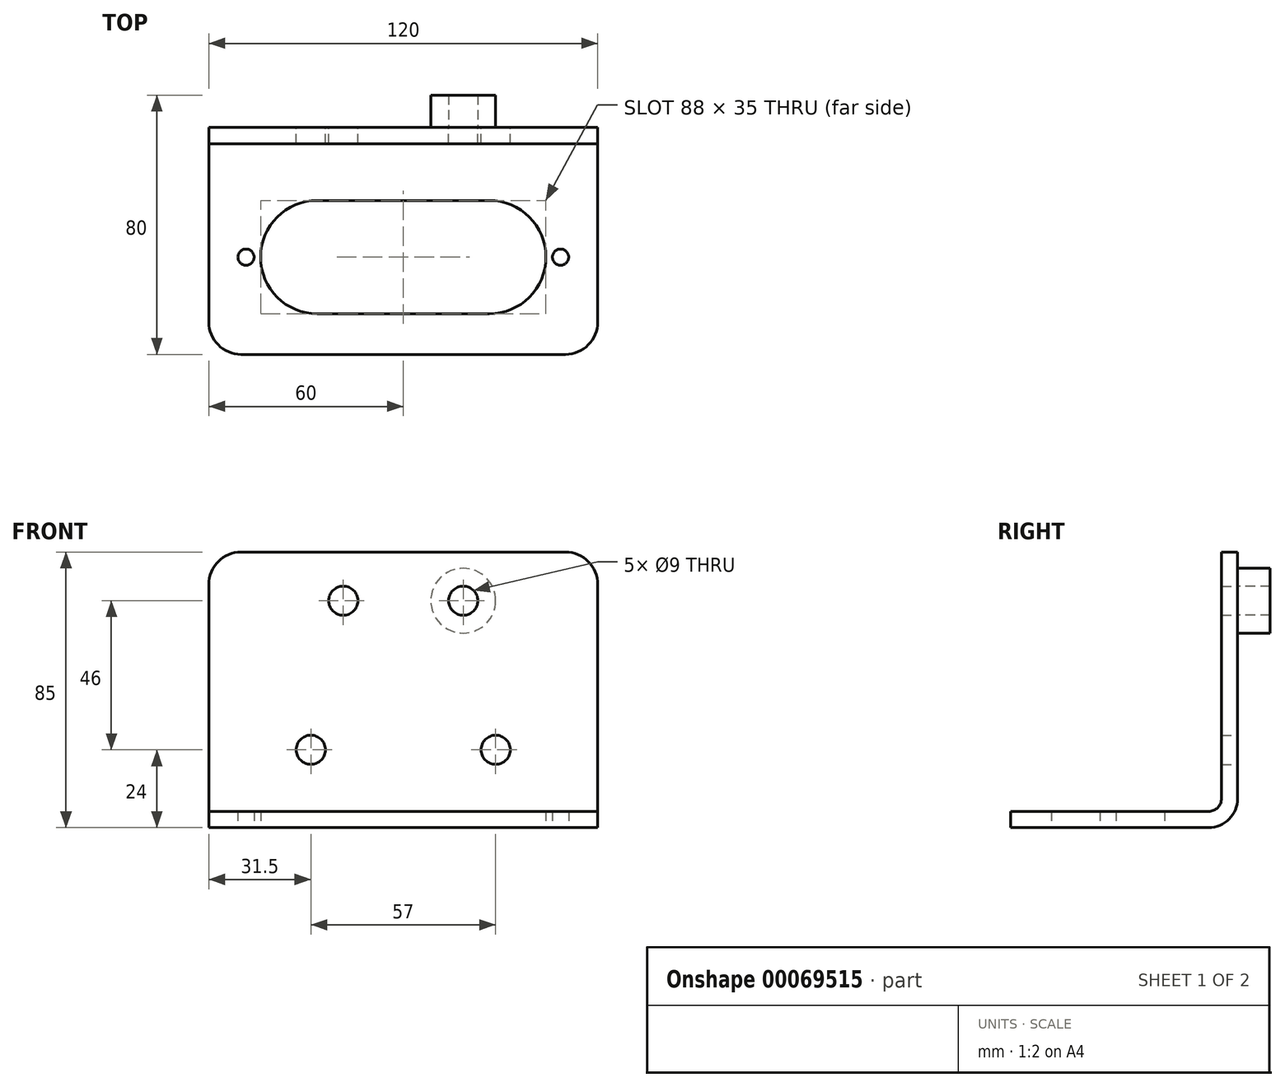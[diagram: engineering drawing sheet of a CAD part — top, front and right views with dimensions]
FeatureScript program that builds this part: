
annotation { "Feature Type Name" : "Feature", "Feature Type Description" : "" }
export const myFeature = defineFeature(function(context is Context, id is Id, definition is map)
    precondition{}
    {
        {
            var Q0;
            Q0=qCreatedBy(makeId("Top.planeOp"),FACE);
            var sketch = newSketch(context, id + "F0", { "sketchPlane" : qUnion([Q0])});
            skLineSegment(sketch, "E0", {"start": v(-60, 0) * mm, "end": v(-60, -60) * mm});
            skArc(sketch, "E1", {"start": v(-60, -60) * mm, "mid": v(-57.07, -67.07) * mm, "end": v(-50, -70) * mm});
            skLineSegment(sketch, "E2", {"start": v(-50, -70) * mm, "end": v(50, -70) * mm});
            skArc(sketch, "E3", {"start": v(50, -70) * mm, "mid": v(57.07, -67.07) * mm, "end": v(60, -60) * mm});
            skLineSegment(sketch, "E4", {"start": v(60, -60) * mm, "end": v(60, 0) * mm});
            skLineSegment(sketch, "E5", {"start": v(60, 0) * mm, "end": v(60, 75) * mm});
            skArc(sketch, "E6", {"start": v(60, 75) * mm, "mid": v(57.07, 82.07) * mm, "end": v(50, 85) * mm});
            skLineSegment(sketch, "E7", {"start": v(50, 85) * mm, "end": v(-50, 85) * mm});
            skArc(sketch, "E8", {"start": v(-50, 85) * mm, "mid": v(-57.07, 82.07) * mm, "end": v(-60, 75) * mm});
            skLineSegment(sketch, "E9", {"start": v(-60, 75) * mm, "end": v(-60, 0) * mm});
            skLineSegment(sketch, "E10", {"start": v(26.5, -22.5) * mm, "end": v(-26.5, -22.5) * mm});
            skArc(sketch, "E11", {"start": v(-26.5, -22.5) * mm, "mid": v(-44, -40) * mm, "end": v(-26.5, -57.5) * mm});
            skLineSegment(sketch, "E12", {"start": v(-26.5, -57.5) * mm, "end": v(26.5, -57.5) * mm});
            skArc(sketch, "E13", {"start": v(26.5, -57.5) * mm, "mid": v(44, -40) * mm, "end": v(26.5, -22.5) * mm});
            skCircle(sketch, "E14", {"center": v(-48.5, -40) * mm, "radius": 2.5 * mm});
            skCircle(sketch, "E15", {"center": v(48.5, -40) * mm, "radius": 2.5 * mm});
            skCircle(sketch, "E16", {"center": v(18.5, 70) * mm, "radius": 4.5 * mm});
            skCircle(sketch, "E17", {"center": v(28.5, 24) * mm, "radius": 4.5 * mm});
            skLineSegment(sketch, "E18", {"start": v(-60, 0) * mm, "end": v(60, 0) * mm});
            skLineSegment(sketch, "E19", {"start": v(-48.5, -40) * mm, "end": v(48.5, -40) * mm, "construction": true});
            skLineSegment(sketch, "E20", {"start": v(0, 85) * mm, "end": v(0, -70) * mm, "construction": true});
            skCircle(sketch, "E21.MirrorC", {"center": v(-18.5, 70) * mm, "radius": 4.5 * mm});
            skCircle(sketch, "E22.MirrorC", {"center": v(-28.5, 24) * mm, "radius": 4.5 * mm});
            skSolve(sketch);
        }
        {
            var Q0;
            Q0=makeQuery(id+"F0.imprint","IMPRINT",FACE,{"disambiguationData":[TD([[makeQuery(id+"F0.imprint","IMPRINT",EDGE,{"derivedFrom":sQuery(id+"F0.wireOp",EDGE,"E0")}),1.0]])]});
            extrude(context, id + "F1", {"entities" : qUnion([Q0]), "depth" : 5 * mm});
        }
        {
            var Q0;
            Q0=makeQuery(id+"F0.imprint","IMPRINT",FACE,{"disambiguationData":[TD([[makeQuery(id+"F0.imprint","IMPRINT",EDGE,{"derivedFrom":sQuery(id+"F0.wireOp",EDGE,"E5")}),1.0]])]});
            extrude(context, id + "F2", {"entities" : qUnion([Q0]), "depth" : 5 * mm});
        }
        {
            var Q0;
            Q0=makeQuery(id+"F2.opExtrude","SWEPT_BODY",BODY,{"disambiguationData":[OSD([sQuery(id+"F0.wireOp",EDGE,"dcd2564a-1519-4e3c-a726-8554a83bfc4d"),sQuery(id+"F0.wireOp",EDGE,"E5"),sQuery(id+"F0.wireOp",EDGE,"E6"),sQuery(id+"F0.wireOp",EDGE,"E7"),sQuery(id+"F0.wireOp",EDGE,"E8"),sQuery(id+"F0.wireOp",EDGE,"E9"),sQuery(id+"F0.wireOp",EDGE,"f265843f-5eec-4993-bfec-df9498e86563"),sQuery(id+"F0.wireOp",EDGE,"E16"),sQuery(id+"F0.wireOp",EDGE,"E17"),sQuery(id+"F0.wireOp",EDGE,"E18")])]});
            var Q1;
            Q1=makeQuery(id+"F1.opExtrude","CAP_EDGE",EDGE,{"disambiguationData":[OSD([sQuery(id+"F0.wireOp",EDGE,"E18")])],"isStart":false});
            transform(context, id + "F3", {"entities" : qUnion([Q0]), "transformType" : TransformType.ROTATION, "transformAxis" : qUnion([Q1]), "angle" : 90 * degree, "makeCopy" : false});
        }
        {
            var Q0;
            Q0=makeQuery(id+"F2.opExtrude","SWEPT_BODY",BODY,{"disambiguationData":[OSD([sQuery(id+"F0.wireOp",EDGE,"dcd2564a-1519-4e3c-a726-8554a83bfc4d"),sQuery(id+"F0.wireOp",EDGE,"E5"),sQuery(id+"F0.wireOp",EDGE,"E6"),sQuery(id+"F0.wireOp",EDGE,"E7"),sQuery(id+"F0.wireOp",EDGE,"E8"),sQuery(id+"F0.wireOp",EDGE,"E9"),sQuery(id+"F0.wireOp",EDGE,"f265843f-5eec-4993-bfec-df9498e86563"),sQuery(id+"F0.wireOp",EDGE,"E16"),sQuery(id+"F0.wireOp",EDGE,"E17"),sQuery(id+"F0.wireOp",EDGE,"E18")])]});
            transform(context, id + "F4", {"entities" : qUnion([Q0]), "transformType" : TransformType.TRANSLATION_3D, "dx" : 0 * mm, "dy" : -5 * mm, "dz" : -5 * mm, "makeCopy" : false});
        }
        {
            var Q0;
            Q0=makeQuery(id+"F1.opExtrude","SWEPT_BODY",BODY,{"disambiguationData":[OSD([sQuery(id+"F0.wireOp",EDGE,"E0"),sQuery(id+"F0.wireOp",EDGE,"E1"),sQuery(id+"F0.wireOp",EDGE,"E2"),sQuery(id+"F0.wireOp",EDGE,"E3"),sQuery(id+"F0.wireOp",EDGE,"E4"),sQuery(id+"F0.wireOp",EDGE,"b944222a-91ae-40db-8da9-c3a74cff1a19"),sQuery(id+"F0.wireOp",EDGE,"52282161-0c92-4602-815b-eede0631a33d"),sQuery(id+"F0.wireOp",EDGE,"E10"),sQuery(id+"F0.wireOp",EDGE,"E11"),sQuery(id+"F0.wireOp",EDGE,"E12"),sQuery(id+"F0.wireOp",EDGE,"E13"),sQuery(id+"F0.wireOp",EDGE,"E14"),sQuery(id+"F0.wireOp",EDGE,"E15"),sQuery(id+"F0.wireOp",EDGE,"E18")])]});
            var Q1;
            Q1=makeQuery(id+"F2.opExtrude","SWEPT_BODY",BODY,{"disambiguationData":[OSD([sQuery(id+"F0.wireOp",EDGE,"dcd2564a-1519-4e3c-a726-8554a83bfc4d"),sQuery(id+"F0.wireOp",EDGE,"E5"),sQuery(id+"F0.wireOp",EDGE,"E6"),sQuery(id+"F0.wireOp",EDGE,"E7"),sQuery(id+"F0.wireOp",EDGE,"E8"),sQuery(id+"F0.wireOp",EDGE,"E9"),sQuery(id+"F0.wireOp",EDGE,"f265843f-5eec-4993-bfec-df9498e86563"),sQuery(id+"F0.wireOp",EDGE,"E16"),sQuery(id+"F0.wireOp",EDGE,"E17"),sQuery(id+"F0.wireOp",EDGE,"E18")])]});
            booleanBodies(context, id + "F5", {"operationType" : BooleanOperationType.UNION, "tools" : qUnion([Q0, Q1])});
        }
        {
            var Q0;
            {var subQ0=sQuery(id+"F0.wireOp",EDGE,"E18");Q0=makeQuery(id+"F5.opBoolean","INTERSECT",EDGE,{"derivedFrom":[makeQuery(id+"F1.opExtrude","CAP_FACE",FACE,{"disambiguationData":[OSD([sQuery(id+"F0.wireOp",EDGE,"E0"),sQuery(id+"F0.wireOp",EDGE,"E1"),sQuery(id+"F0.wireOp",EDGE,"E2"),sQuery(id+"F0.wireOp",EDGE,"E3"),sQuery(id+"F0.wireOp",EDGE,"E4"),sQuery(id+"F0.wireOp",EDGE,"b944222a-91ae-40db-8da9-c3a74cff1a19"),sQuery(id+"F0.wireOp",EDGE,"52282161-0c92-4602-815b-eede0631a33d"),sQuery(id+"F0.wireOp",EDGE,"E10"),sQuery(id+"F0.wireOp",EDGE,"E11"),sQuery(id+"F0.wireOp",EDGE,"E12"),sQuery(id+"F0.wireOp",EDGE,"E13"),sQuery(id+"F0.wireOp",EDGE,"E14"),sQuery(id+"F0.wireOp",EDGE,"E15"),subQ0])],"isStart":false}),makeQuery(id+"F2.opExtrude","CAP_FACE",FACE,{"disambiguationData":[OSD([sQuery(id+"F0.wireOp",EDGE,"dcd2564a-1519-4e3c-a726-8554a83bfc4d"),sQuery(id+"F0.wireOp",EDGE,"E5"),sQuery(id+"F0.wireOp",EDGE,"E6"),sQuery(id+"F0.wireOp",EDGE,"E7"),sQuery(id+"F0.wireOp",EDGE,"E8"),sQuery(id+"F0.wireOp",EDGE,"E9"),sQuery(id+"F0.wireOp",EDGE,"f265843f-5eec-4993-bfec-df9498e86563"),sQuery(id+"F0.wireOp",EDGE,"E16"),sQuery(id+"F0.wireOp",EDGE,"E17"),subQ0])],"isStart":false})]});}
            fillet(context, id + "F6", {"entities" : qUnion([Q0]), "radius" : 4 * mm, "tangentPropagation" : true, "allowEdgeOverflow" : false});
        }
        {
            var Q0;
            Q0=makeQuery(id+"F1.opExtrude","CAP_EDGE",EDGE,{"disambiguationData":[OSD([sQuery(id+"F0.wireOp",EDGE,"E18")])],"isStart":true});
            fillet(context, id + "F7", {"entities" : qUnion([Q0]), "radius" : 9 * mm, "tangentPropagation" : true, "allowEdgeOverflow" : false});
        }
        {
            var Q0;
            {var subQ0=sQuery(id+"F0.wireOp",EDGE,"E18");Q0=makeQuery(id+"F5.opBoolean","MERGE",FACE,{"derivedFrom":[makeQuery(id+"F1.opExtrude","SWEPT_FACE",FACE,{"disambiguationData":[OSD([subQ0])]}),makeQuery(id+"F2.opExtrude","CAP_FACE",FACE,{"disambiguationData":[OSD([sQuery(id+"F0.wireOp",EDGE,"E5"),sQuery(id+"F0.wireOp",EDGE,"E6"),sQuery(id+"F0.wireOp",EDGE,"E7"),sQuery(id+"F0.wireOp",EDGE,"E8"),sQuery(id+"F0.wireOp",EDGE,"E9"),sQuery(id+"F0.wireOp",EDGE,"E16"),sQuery(id+"F0.wireOp",EDGE,"E17"),subQ0])],"isStart":true})]});}
            var sketch = newSketch(context, id + "F8", { "sketchPlane" : qUnion([Q0])});
            skCircle(sketch, "E23.0", {"center": v(-18.5, 70) * mm, "radius": 4.5 * mm});
            skCircle(sketch, "E24", {"center": v(-18.5, 70) * mm, "radius": 10 * mm});
            skSolve(sketch);
        }
        {
            var Q0;
            Q0 = qSketchRegion(id + "F8", true);
            extrude(context, id + "F9", {"entities" : qUnion([Q0]), "depth" : 10 * mm});
        }
    });
